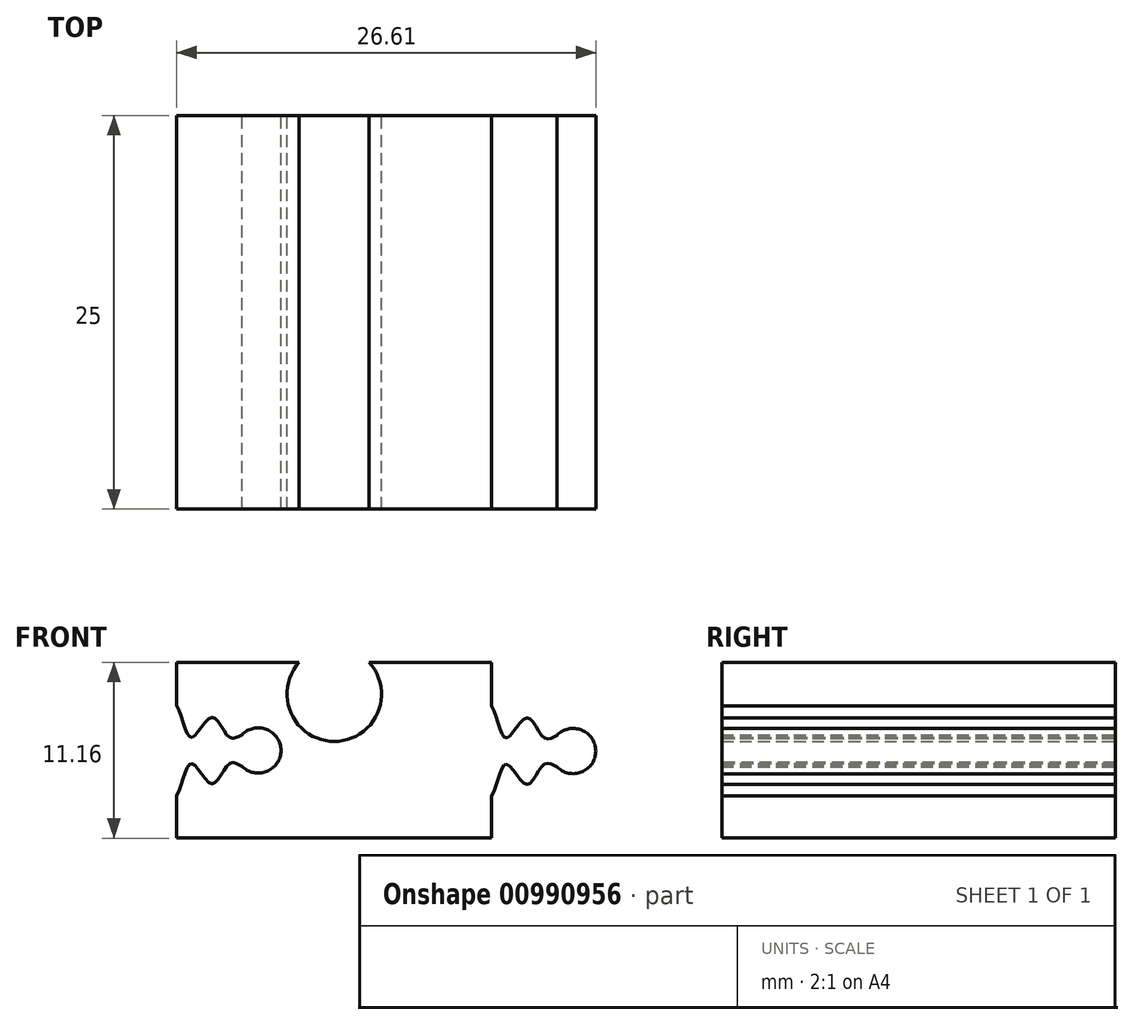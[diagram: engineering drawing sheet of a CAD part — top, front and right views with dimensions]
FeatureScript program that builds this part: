
annotation { "Feature Type Name" : "Feature", "Feature Type Description" : "" }
export const myFeature = defineFeature(function(context is Context, id is Id, definition is map)
    precondition{}
    {
        {
            var Q0;
            Q0=qCreatedBy(makeId("Front.planeOp"),FACE);
            var sketch = newSketch(context, id + "F0", { "sketchPlane" : qUnion([Q0])});
            skLineSegment(sketch, "E0.bottom", {"start": v(10, -5.58) * mm, "end": v(-10, -5.58) * mm});
            skLineSegment(sketch, "E0.top", {"start": v(10, 5.58) * mm, "end": v(-10, 5.58) * mm});
            skLineSegment(sketch, "E0.left", {"start": v(10, -5.58) * mm, "end": v(10, 5.58) * mm});
            skLineSegment(sketch, "E0.right", {"start": v(-10, -5.58) * mm, "end": v(-10, 5.58) * mm});
            skPoint(sketch, "E0.middle", {"position": v(0, 0) * mm});
            skPoint(sketch, "E1", {"position": v(0, -0.01) * mm});
            skPoint(sketch, "E2", {"position": v(0, 3.56) * mm});
            skCircle(sketch, "E3", {"center": v(0, 3.56) * mm, "radius": 3 * mm});
            skLineSegment(sketch, "E4", {"start": v(0, -0.01) * mm, "end": v(-15.55, -0.01) * mm, "construction": true});
            skLineSegment(sketch, "E5", {"start": v(0, 0) * mm, "end": v(-12.37, 0) * mm, "construction": true});
            skLineSegment(sketch, "E6", {"start": v(0, 13.33) * mm, "end": v(0, -12.08) * mm, "construction": true});
            skLineSegment(sketch, "E7.MirrorCS", {"start": v(0, 0) * mm, "end": v(12.37, 0) * mm, "construction": true});
            skLineSegment(sketch, "E8.MirrorCS", {"start": v(0, -0.01) * mm, "end": v(15.55, -0.01) * mm, "construction": true});
            skFitSpline(sketch, "E9", {"points": [v(-10, 2.84) * mm, v(-9.07, 0.83) * mm, v(-7.78, 2.1) * mm, v(-6.65, 0.83) * mm, v(-5.86, 0.99) * mm], "startDerivative": vector(3.32, -5.63) * mm, "endDerivative": vector(3.67, 1.92) * mm});
            skFitSpline(sketch, "E10.MirrorCS", {"points": [v(-10, -2.86) * mm, v(-9.07, -0.85) * mm, v(-7.78, -2.12) * mm, v(-6.65, -0.85) * mm, v(-5.86, -1) * mm], "startDerivative": vector(3.32, 5.63) * mm, "endDerivative": vector(3.67, -1.92) * mm});
            skArc(sketch, "E11", {"start": v(-5.86, -1) * mm, "mid": v(-3.4, -0.01) * mm, "end": v(-5.86, 0.99) * mm});
            skFitSpline(sketch, "E12", {"points": [v(10, 2.8) * mm, v(10.93, 0.79) * mm, v(12.22, 2.06) * mm, v(13.35, 0.79) * mm, v(14.14, 0.95) * mm], "startDerivative": vector(3.32, -5.63) * mm, "endDerivative": vector(3.67, 1.92) * mm});
            skFitSpline(sketch, "E13.MirrorCS", {"points": [v(10, -2.9) * mm, v(10.93, -0.88) * mm, v(12.22, -2.16) * mm, v(13.35, -0.88) * mm, v(14.14, -1.05) * mm], "startDerivative": vector(3.32, 5.63) * mm, "endDerivative": vector(3.67, -1.92) * mm});
            skArc(sketch, "E14", {"start": v(14.14, -1.05) * mm, "mid": v(16.6, -0.05) * mm, "end": v(14.14, 0.95) * mm});
            skSolve(sketch);
        }
        {
            var Q0;
            {var subQ0=sQuery(id+"F0.wireOp",EDGE,"5b1f0303-7e19-4a52-9026-6a9802054e040.MirrorCS");Q0=makeQuery(id+"F0.imprint","IMPRINT",FACE,{"disambiguationData":[TD([[makeQuery(id+"F0.imprint","IMPRINT",EDGE,{"derivedFrom":subQ0}),1.0]])]});}
            var Q1;
            {var subQ0=sQuery(id+"F0.wireOp",EDGE,"cc34c8df-07c0-4cc4-8682-5ab28225645b0.MirrorCS");Q1=makeQuery(id+"F0.imprint","IMPRINT",FACE,{"disambiguationData":[TD([[makeQuery(id+"F0.imprint","IMPRINT",EDGE,{"derivedFrom":subQ0}),1.0]])]});}
            var Q2;
            {var subQ1=sQuery(id+"F0.wireOp",EDGE,"474448f5-d81b-42c5-8d5d-bf9c72034bf10.MirrorCS");Q2=makeQuery(id+"F0.imprint","IMPRINT",FACE,{"disambiguationData":[TD([[makeQuery(id+"F0.imprint","IMPRINT",EDGE,{"derivedFrom":subQ1}),-1.0]])]});}
            var Q3;
            {var subQ9=sQuery(id+"F0.wireOp",EDGE,"E0.bottom");Q3=makeQuery(id+"F0.imprint","IMPRINT",FACE,{"disambiguationData":[TD([[makeQuery(id+"F0.imprint","IMPRINT",EDGE,{"derivedFrom":subQ9}),-1.0]])]});}
            var Q4;
            {var subQ0=sQuery(id+"F0.wireOp",EDGE,"E12");Q4=makeQuery(id+"F0.imprint","IMPRINT",FACE,{"disambiguationData":[TD([[makeQuery(id+"F0.imprint","IMPRINT",EDGE,{"derivedFrom":subQ0}),-1.0]])]});}
            extrude(context, id + "F1", {"entities" : qUnion([Q0, Q1, Q2, Q3, Q4]), "depth" : 25 * mm, "offsetDistance" : 25 * mm});
        }
    });
